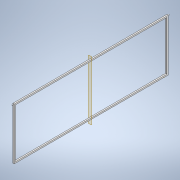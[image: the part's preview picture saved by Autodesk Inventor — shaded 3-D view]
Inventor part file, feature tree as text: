
AUTODESK INVENTOR PART (.ipt)
format: ipt  version: 2022 (Build 260153000, 153)  size: 180,736 bytes
history: native  units: mm
features: extrude x7, sketch x7, projected_geometry x3, plane x2, mirror x2, fillet x1
ambient origin geometry x8: Origin, YZ Plane, XZ Plane, XY Plane, X Axis, Y Axis, Z Axis, Center Point
bodies: Solid1 (feature_tree)
feature tree (22):
  extrude  "Extrusion1"  Depth=10.0mm
  extrude  "Extrusion2"  Depth=10.0mm
  plane  "Work Plane1"
  mirror  "Mirror1"
  fillet  "Fillet1"  [1 undecoded]
  plane  "Work Plane2"
  extrude  "Extrusion3"  Depth=35.0mm TaperAngle=0.0deg
  extrude  "Extrusion4"  Depth=10.0mm
  extrude  "Extrusion5"  Depth=15.0mm TaperAngle=0.0deg
  extrude  "Extrusion6"  Depth=10.0mm TaperAngle=0.0deg
  extrude  "Extrusion7"  Depth=10.0mm TaperAngle=0.0deg
  mirror  "Mirror2"
  sketch  "Sketch1"  dims[d0=383.0mm d2=10.0mm]
  sketch  "Sketch2"  dims[d3=10.0mm d4=0.0mm d5=4.5mm d6=135.0deg]
  projected_geometry  "Projected Loop1"
  sketch  "Sketch3"  dims[d7=1.0mm d8=35.0mm d9=0.0mm]
  sketch  "Sketch4"  dims[d10=10.0mm d11=2.0mm]
  sketch  "Sketch5"  dims[d12=-10.0mm d13=15.0mm d14=0.0mm]
  sketch  "Sketch6"  dims[d15=10.0mm d16=0.0mm d17=10.0mm d18=0.0mm]
  projected_geometry  "Projected Loop2"
  sketch  "Sketch7"  dims[d19=5.0mm d20=10.0mm d21=0.0mm d22=10.0mm d23=5.0mm d24=0.0mm]
  projected_geometry  "Projected Loop3"
note: 1 required parameter value undecoded (feature->parameter linkage not recoverable at this tier; creation-order binding heuristic only, values carry confidence <= 0.55)
